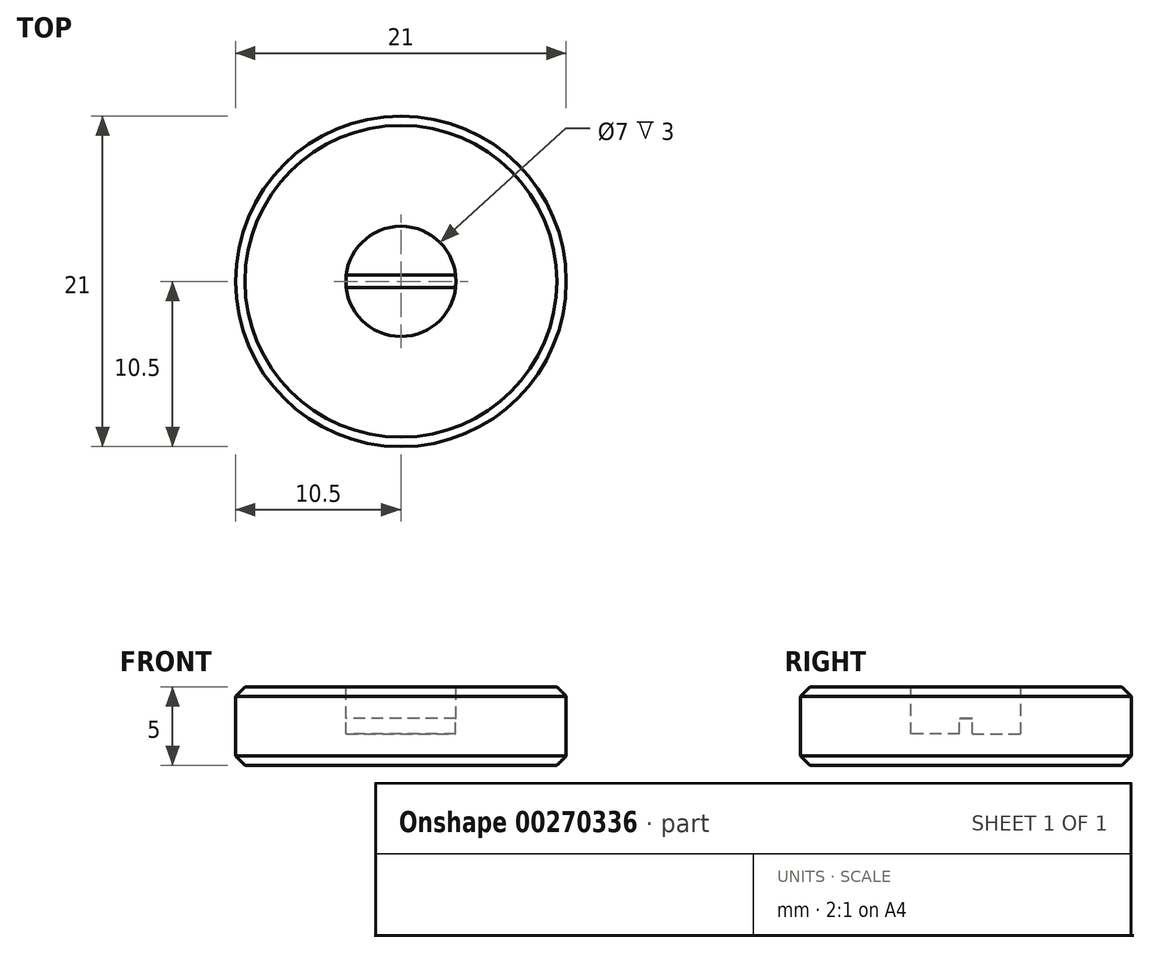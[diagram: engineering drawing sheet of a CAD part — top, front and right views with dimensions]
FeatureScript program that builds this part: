
annotation { "Feature Type Name" : "Feature", "Feature Type Description" : "" }
export const myFeature = defineFeature(function(context is Context, id is Id, definition is map)
    precondition{}
    {
        {
            var Q0;
            Q0=qCreatedBy(makeId("Top.planeOp"),FACE);
            var sketch = newSketch(context, id + "F0", { "sketchPlane" : qUnion([Q0])});
            skCircle(sketch, "E0", {"center": v(0, 0) * mm, "radius": 10.5 * mm});
            skSolve(sketch);
        }
        {
            var Q0;
            Q0 = qSketchRegion(id + "F0", true);
            extrude(context, id + "F1", {"entities" : qUnion([Q0]), "depth" : 5 * mm});
        }
        {
            var Q0;
            Q0=makeQuery(id+"F1.opExtrude","CAP_FACE",FACE,{"disambiguationData":[OSD([sQuery(id+"F0.wireOp",EDGE,"E0")])],"isStart":false});
            var sketch = newSketch(context, id + "F2", { "sketchPlane" : qUnion([Q0])});
            skCircle(sketch, "E1", {"center": v(0, 0) * mm, "radius": 3.5 * mm});
            skSolve(sketch);
        }
        {
            var Q0;
            Q0 = qSketchRegion(id + "F2", true);
            extrude(context, id + "F3", {"entities" : qUnion([Q0]), "operationType" : NewBodyOperationType.REMOVE, "oppositeDirection" : true, "depth" : 3 * mm});
        }
        {
            var Q0;
            Q0=makeQuery(id+"F3.boolean.opBoolean","COPY",FACE,{"derivedFrom":makeQuery(id+"F3.opExtrude","CAP_FACE",FACE,{"disambiguationData":[OSD([sQuery(id+"F2.wireOp",EDGE,"E1")])],"isStart":false})});
            var sketch = newSketch(context, id + "F4", { "sketchPlane" : qUnion([Q0])});
            skLineSegment(sketch, "E2.bottom", {"start": v(4, -0.4) * mm, "end": v(-4, -0.4) * mm});
            skLineSegment(sketch, "E2.top", {"start": v(4, 0.4) * mm, "end": v(-4, 0.4) * mm});
            skLineSegment(sketch, "E2.left", {"start": v(4, -0.4) * mm, "end": v(4, 0.4) * mm});
            skLineSegment(sketch, "E2.right", {"start": v(-4, -0.4) * mm, "end": v(-4, 0.4) * mm});
            skPoint(sketch, "E2.middle", {"position": v(0, 0) * mm});
            skSolve(sketch);
        }
        {
            var Q0;
            Q0 = qSketchRegion(id + "F4", true);
            extrude(context, id + "F5", {"entities" : qUnion([Q0]), "operationType" : NewBodyOperationType.ADD, "depth" : 1 * mm});
        }
        {
            var Q0;
            Q0=makeQuery(id+"F1.opExtrude","CAP_EDGE",EDGE,{"disambiguationData":[OSD([sQuery(id+"F0.wireOp",EDGE,"E0")])],"isStart":false});
            var Q1;
            Q1=makeQuery(id+"F1.opExtrude","CAP_EDGE",EDGE,{"disambiguationData":[OSD([sQuery(id+"F0.wireOp",EDGE,"E0")])],"isStart":true});
            chamfer(context, id + "F6", {"entities" : qUnion([Q0, Q1]), "width" : 0.6 * mm, "tangentPropagation" : true});
        }
    });
